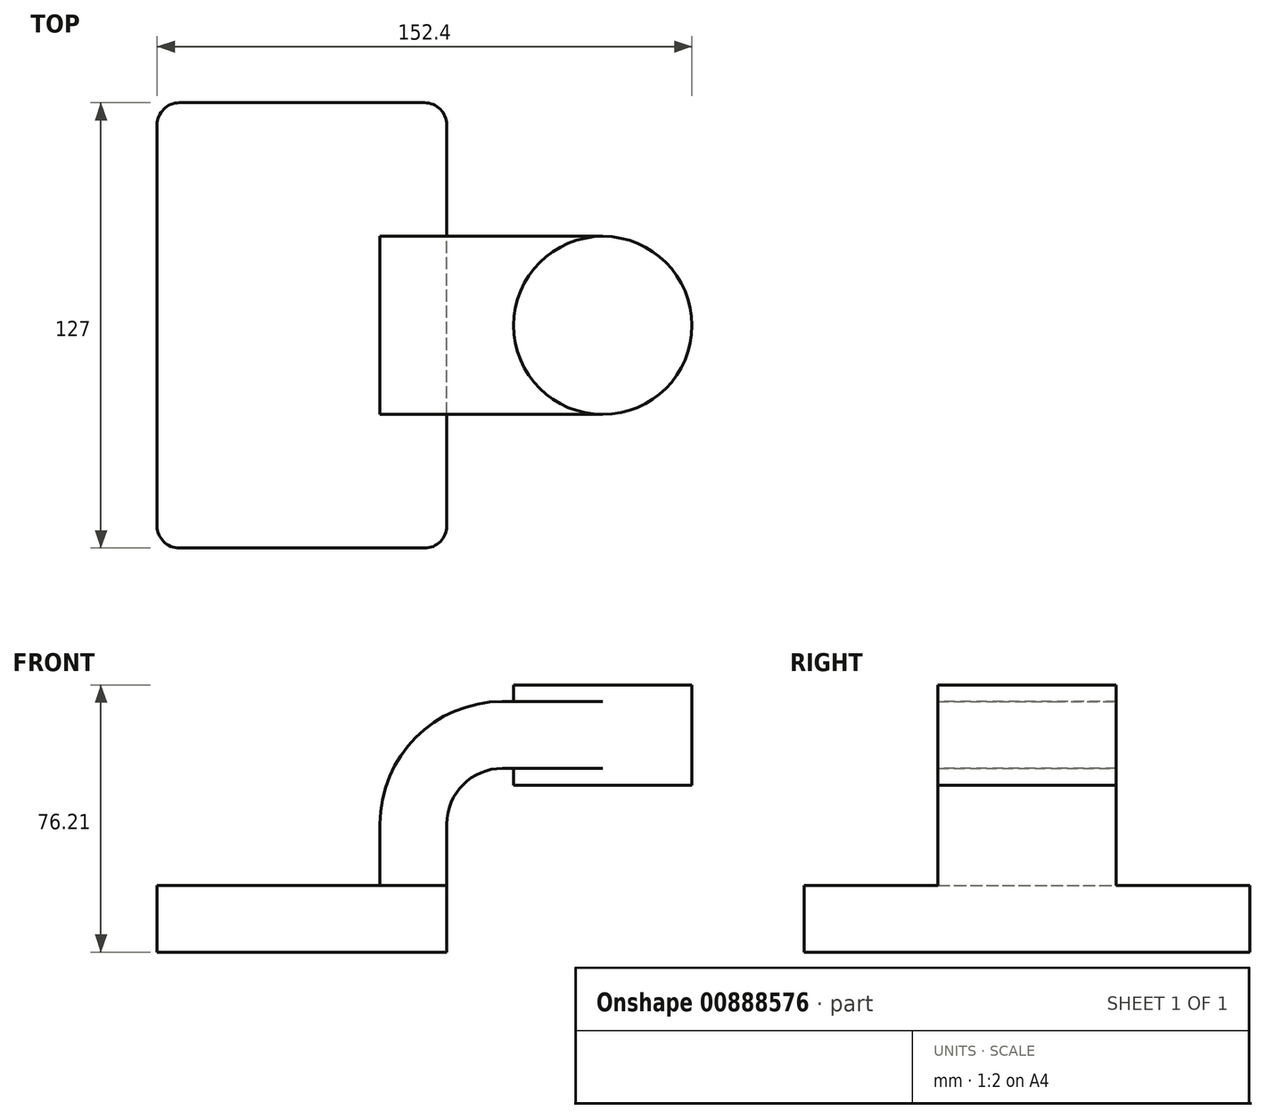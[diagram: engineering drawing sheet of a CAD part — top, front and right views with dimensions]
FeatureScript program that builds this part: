
annotation { "Feature Type Name" : "Feature", "Feature Type Description" : "" }
export const myFeature = defineFeature(function(context is Context, id is Id, definition is map)
    precondition{}
    {
        {
            var Q0;
            Q0=qCreatedBy(makeId("Front.planeOp"),FACE);
            var sketch = newSketch(context, id + "F0", { "sketchPlane" : qUnion([Q0])});
            skLineSegment(sketch, "E0.bottom", {"start": v(-41.28, -9.53) * mm, "end": v(41.28, -9.53) * mm});
            skLineSegment(sketch, "E0.top", {"start": v(-41.28, 9.52) * mm, "end": v(41.28, 9.52) * mm});
            skLineSegment(sketch, "E0.left", {"start": v(-41.27, -9.53) * mm, "end": v(-41.28, 9.52) * mm});
            skLineSegment(sketch, "E0.right", {"start": v(41.28, -9.53) * mm, "end": v(41.28, 9.52) * mm});
            skPoint(sketch, "E0.middle", {"position": v(0, 0) * mm});
            skLineSegment(sketch, "E1.bottom", {"start": v(60.32, 38.1) * mm, "end": v(111.12, 38.1) * mm});
            skLineSegment(sketch, "E1.top", {"start": v(60.32, 66.67) * mm, "end": v(111.12, 66.67) * mm});
            skLineSegment(sketch, "E1.left", {"start": v(60.32, 38.1) * mm, "end": v(60.32, 66.67) * mm});
            skLineSegment(sketch, "E1.right", {"start": v(111.12, 38.1) * mm, "end": v(111.12, 66.67) * mm});
            skPoint(sketch, "E1.middle", {"position": v(85.72, 52.39) * mm});
            skLineSegment(sketch, "E2", {"start": v(41.27, 9.52) * mm, "end": v(41.27, 27) * mm});
            skArc(sketch, "E3", {"start": v(41.27, 27) * mm, "mid": v(45.92, 38.23) * mm, "end": v(57.15, 42.88) * mm});
            skLineSegment(sketch, "E4", {"start": v(57.15, 42.88) * mm, "end": v(85.72, 42.88) * mm});
            skLineSegment(sketch, "E5.0", {"start": v(57.15, 61.93) * mm, "end": v(85.72, 61.93) * mm});
            skArc(sketch, "E5.1", {"start": v(22.22, 27) * mm, "mid": v(32.45, 51.7) * mm, "end": v(57.15, 61.93) * mm});
            skLineSegment(sketch, "E5.2", {"start": v(22.22, 9.52) * mm, "end": v(22.22, 27) * mm});
            skLineSegment(sketch, "E6", {"start": v(85.72, 66.67) * mm, "end": v(85.72, 38.1) * mm});
            skFitSpline(sketch, "E7", {"points": [v(-41.28, 9.53) * mm, v(57.15, 61.93) * mm], "startDerivative": vector(0.04, 138.31) * mm, "endDerivative": vector(114.24, 0.2) * mm});
            skSolve(sketch);
        }
        {
            var Q0;
            Q0=makeQuery(id+"F0.imprint","IMPRINT",FACE,{"disambiguationData":[TD([[makeQuery(id+"F0.imprint","IMPRINT",EDGE,{"derivedFrom":sQuery(id+"F0.wireOp",EDGE,"E0.bottom")}),1.0]])]});
            extrude(context, id + "F1", {"entities" : qUnion([Q0]), "endBound" : BoundingType.SYMMETRIC, "depth" : 127 * mm, "offsetDistance" : 25.4 * mm});
        }
        {
            var Q0;
            {var subQ5=sQuery(id+"F0.wireOp",EDGE,"E2");Q0=makeQuery(id+"F0.imprint","IMPRINT",FACE,{"disambiguationData":[TD([[makeQuery(id+"F0.imprint","IMPRINT",EDGE,{"derivedFrom":subQ5}),1.0]])]});}
            var Q1;
            {var subQ0=sQuery(id+"F0.wireOp",EDGE,"E4");var subQ1=sQuery(id+"F0.wireOp",EDGE,"E1.left");var subQ2=makeQuery(id+"F0.imprint","INTERSECT",VERTEX,{"derivedFrom":[subQ1,subQ0]});Q1=makeQuery(id+"F0.imprint","IMPRINT",FACE,{"disambiguationData":[TD([[makeQuery(id+"F0.imprint","IMPRINT",EDGE,{"disambiguationData":[TD([[subQ2,-1.0]])],"derivedFrom":subQ1}),-1.0]])]});}
            extrude(context, id + "F2", {"entities" : qUnion([Q0, Q1]), "operationType" : NewBodyOperationType.ADD, "endBound" : BoundingType.SYMMETRIC, "depth" : 50.8 * mm, "offsetDistance" : 25.4 * mm});
        }
        {
            var Q0;
            {var subQ4=sQuery(id+"F0.wireOp",EDGE,"E5.1");Q0=makeQuery(id+"F0.imprint","IMPRINT",FACE,{"disambiguationData":[TD([[makeQuery(id+"F0.imprint","IMPRINT",EDGE,{"derivedFrom":subQ4}),1.0]])]});}
            extrude(context, id + "F3", {"entities" : qUnion([Q0]), "operationType" : NewBodyOperationType.ADD, "endBound" : BoundingType.SYMMETRIC, "depth" : 15.88 * mm, "offsetDistance" : 25.4 * mm});
        }
        {
            var Q0;
            {var subQ0=sQuery(id+"F0.wireOp",EDGE,"E1.right");Q0=makeQuery(id+"F0.imprint","IMPRINT",FACE,{"disambiguationData":[TD([[makeQuery(id+"F0.imprint","IMPRINT",EDGE,{"derivedFrom":subQ0}),1.0]])]});}
            var Q1;
            Q1=sQuery(id+"F0.wireOp",EDGE,"E6");
            revolve(context, id + "F4", {"operationType" : NewBodyOperationType.ADD, "surfaceOperationType" : NewSurfaceOperationType.NEW, "entities" : qUnion([Q0]), "axis" : qUnion([Q1]), "revolveType" : RevolveType.FULL});
        }
        {
            var Q0;
            Q0=makeQuery(id+"F1.opExtrude","CAP_EDGE",EDGE,{"disambiguationData":[OSD([sQuery(id+"F0.wireOp",EDGE,"E0.left")])],"isStart":false});
            var Q1;
            Q1=makeQuery(id+"F1.opExtrude","CAP_EDGE",EDGE,{"disambiguationData":[OSD([sQuery(id+"F0.wireOp",EDGE,"E0.right")])],"isStart":true});
            var Q2;
            Q2=makeQuery(id+"F1.opExtrude","CAP_EDGE",EDGE,{"disambiguationData":[OSD([sQuery(id+"F0.wireOp",EDGE,"E0.right")])],"isStart":false});
            var Q3;
            Q3=makeQuery(id+"F1.opExtrude","CAP_EDGE",EDGE,{"disambiguationData":[OSD([sQuery(id+"F0.wireOp",EDGE,"E0.left")])],"isStart":true});
            fillet(context, id + "F5", {"entities" : qUnion([Q0, Q1, Q2, Q3]), "radius" : 6.35 * mm, "tangentPropagation" : true, "allowEdgeOverflow" : false});
        }
    });
